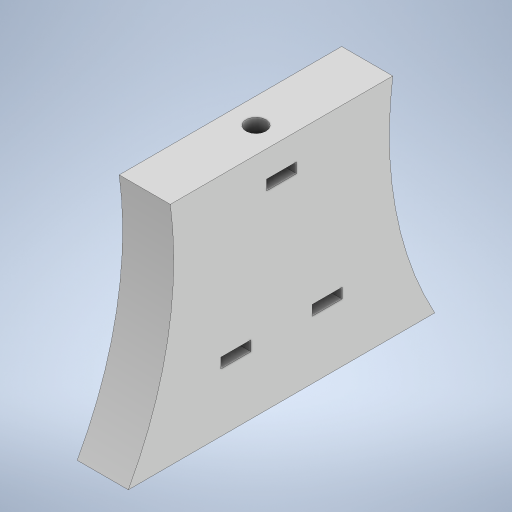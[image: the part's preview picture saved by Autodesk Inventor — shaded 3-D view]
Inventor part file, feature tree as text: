
AUTODESK INVENTOR PART (.ipt)
format: ipt  version: 2023.2 (Build 272271030, 271C)  size: 262,144 bytes
history: native  units: mm
features: extrude x4, sketch x4, projected_geometry x3
ambient origin geometry x8: Origin, YZ Plane, XZ Plane, XY Plane, X Axis, Y Axis, Z Axis, Center Point
bodies: Solid1 (feature_tree)
feature tree (11):
  extrude  "Extrusion1"  Depth=62.0mm
  extrude  "Extrusion2"  Depth=60.963528mm
  extrude  "Extrusion3"  Depth=8.2mm
  extrude  "Extrusion4"  Depth=16.0mm
  sketch  "Sketch1"  dims[d0=200.0mm d1=62.0mm]
  sketch  "Sketch2"  dims[d2=84.0mm d3=60.963528mm]
  projected_geometry  "Projected Loop1"
  sketch  "Sketch3"  dims[d4=14.0mm d5=0.0mm d6=8.2mm]
  projected_geometry  "Projected Loop2"
  sketch  "Sketch4"  dims[d7=2.8mm d8=16.0mm d9=25.0mm d10=14.0mm d11=0.0mm d12=5.5mm d13=25.0mm d14=25.0mm d15=0.0mm d16=8.2mm d17=2.8mm d19=10.0mm d20=5.5mm d21=15.0mm d22=0.0mm]
  projected_geometry  "Projected Loop3"
